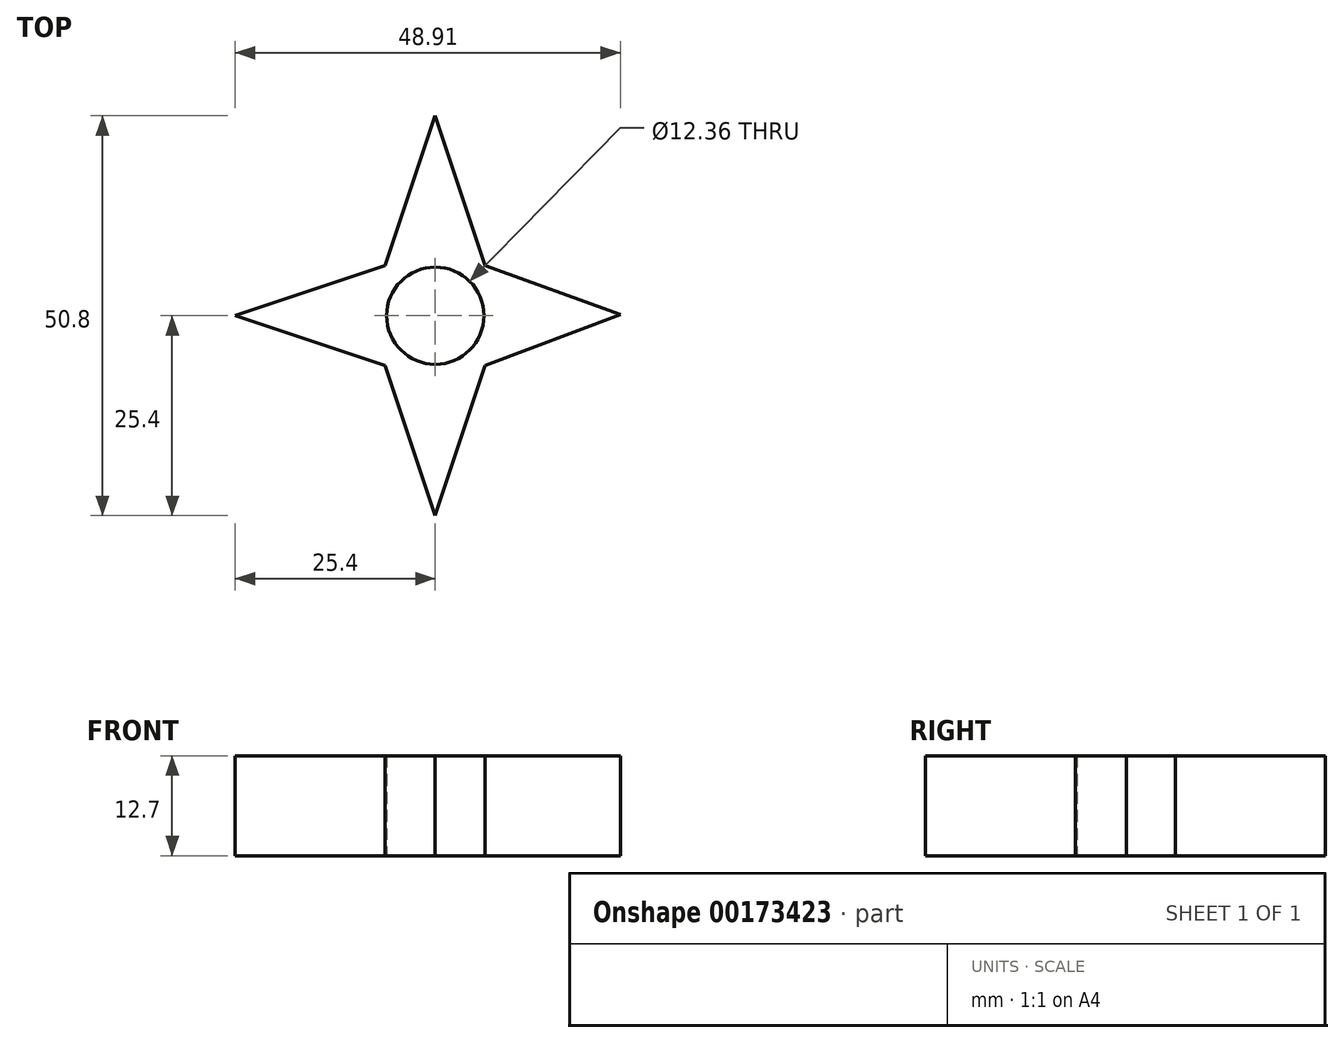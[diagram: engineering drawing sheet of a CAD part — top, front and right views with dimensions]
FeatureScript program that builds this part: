
annotation { "Feature Type Name" : "Feature", "Feature Type Description" : "" }
export const myFeature = defineFeature(function(context is Context, id is Id, definition is map)
    precondition{}
    {
        {
            var Q0;
            Q0=qCreatedBy(makeId("Top.planeOp"),FACE);
            var sketch = newSketch(context, id + "F0", { "sketchPlane" : qUnion([Q0])});
            skLineSegment(sketch, "E0", {"start": v(23.17, 0) * mm, "end": v(23.87, 0) * mm});
            skPoint(sketch, "E1.middle", {"position": v(0, 0) * mm});
            skLineSegment(sketch, "E2", {"start": v(-6.35, 6.35) * mm, "end": v(-25.4, 0) * mm});
            skLineSegment(sketch, "E3", {"start": v(0, 25.4) * mm, "end": v(-6.35, 6.35) * mm});
            skLineSegment(sketch, "E4", {"start": v(0, 25.4) * mm, "end": v(6.35, 6.35) * mm});
            skLineSegment(sketch, "E5", {"start": v(6.35, 6.35) * mm, "end": v(23.87, 0) * mm});
            skLineSegment(sketch, "E6", {"start": v(23.54, 0.14) * mm, "end": v(6.35, -6.35) * mm});
            skLineSegment(sketch, "E7", {"start": v(6.35, -6.35) * mm, "end": v(0, -25.4) * mm});
            skLineSegment(sketch, "E8", {"start": v(0, -25.4) * mm, "end": v(-6.35, -6.35) * mm});
            skLineSegment(sketch, "E9", {"start": v(-6.35, -6.35) * mm, "end": v(-25.4, 0) * mm});
            skCircle(sketch, "E10", {"center": v(0, 0) * mm, "radius": 6.18 * mm});
            skSolve(sketch);
        }
        {
            var Q0;
            Q0=makeQuery(id+"F0.imprint","IMPRINT",FACE,{"disambiguationData":[TD([[makeQuery(id+"F0.imprint","IMPRINT",EDGE,{"derivedFrom":sQuery(id+"F0.wireOp",EDGE,"E2")}),1.0]])]});
            extrude(context, id + "F1", {"entities" : qUnion([Q0]), "depth" : 12.7 * mm});
        }
    });
